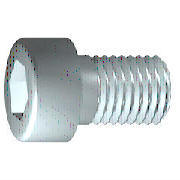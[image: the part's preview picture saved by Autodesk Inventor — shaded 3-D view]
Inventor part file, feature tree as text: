
AUTODESK INVENTOR PART (.ipt)
format: ipt  version: 2022 (Build 260153000, 153)  size: 193,536 bytes
history: native  units: mm (DEFAULTED — no unit token found)
features: sketch x2, other x1, extrude x1, plane x1, fillet x1
ambient origin geometry x7: Origin, YZ Plane, XY Plane, X Axis, Y Axis, Z Axis, Center Point
bodies: Solid1 (feature_tree)
feature tree (6):
  other  "Базовый элемент"
  extrude  "Паз"  Depth=8.875mm
  plane  "Work Plane1"
  fillet  "Fillet2"  Radius=0.276153mm
  sketch  "Эскиз1"
  sketch  "Эскиз2"
